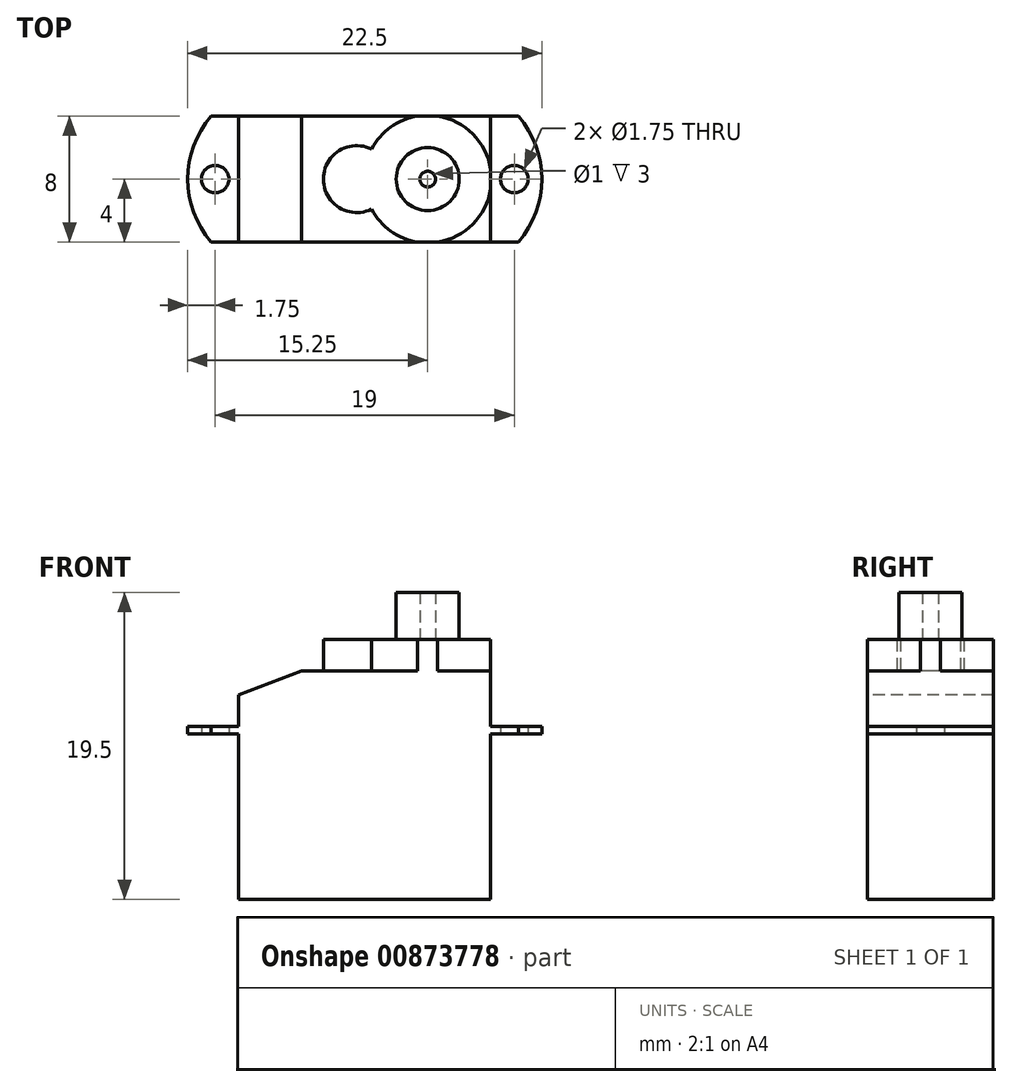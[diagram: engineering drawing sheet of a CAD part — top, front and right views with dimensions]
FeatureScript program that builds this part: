
annotation { "Feature Type Name" : "Feature", "Feature Type Description" : "" }
export const myFeature = defineFeature(function(context is Context, id is Id, definition is map)
    precondition{}
    {
        {
            var Q0;
            Q0=qCreatedBy(makeId("Top.planeOp"),FACE);
            var sketch = newSketch(context, id + "F0", { "sketchPlane" : qUnion([Q0])});
            skLineSegment(sketch, "E0.bottom", {"start": v(8, 4) * mm, "end": v(-8, 4) * mm});
            skLineSegment(sketch, "E0.top", {"start": v(8, -4) * mm, "end": v(-8, -4) * mm});
            skLineSegment(sketch, "E0.left", {"start": v(8, 4) * mm, "end": v(8, -4) * mm});
            skLineSegment(sketch, "E0.right", {"start": v(-8, 4) * mm, "end": v(-8, -4) * mm});
            skPoint(sketch, "E0.middle", {"position": v(0, 0) * mm});
            skSolve(sketch);
        }
        {
            var Q0;
            Q0 = qSketchRegion(id + "F0", true);
            extrude(context, id + "F1", {"entities" : qUnion([Q0]), "depth" : 10.5 * mm, "offsetDistance" : 25 * mm});
        }
        {
            var Q0;
            Q0=makeQuery(id+"F1.opExtrude","CAP_FACE",FACE,{"disambiguationData":[OSD([sQuery(id+"F0.wireOp",EDGE,"E0.bottom"),sQuery(id+"F0.wireOp",EDGE,"E0.top"),sQuery(id+"F0.wireOp",EDGE,"E0.left"),sQuery(id+"F0.wireOp",EDGE,"E0.right")])],"isStart":false});
            var sketch = newSketch(context, id + "F2", { "sketchPlane" : qUnion([Q0])});
            skLineSegment(sketch, "E1.bottom", {"start": v(9.75, 4) * mm, "end": v(-9.75, 4) * mm});
            skLineSegment(sketch, "E1.top", {"start": v(9.75, -4) * mm, "end": v(-9.75, -4) * mm});
            skPoint(sketch, "E1.middle", {"position": v(0, 0) * mm});
            skArc(sketch, "E2", {"start": v(-9.75, 4) * mm, "mid": v(-11.25, 0) * mm, "end": v(-9.75, -4) * mm});
            skArc(sketch, "E3", {"start": v(9.75, -4) * mm, "mid": v(11.25, 0) * mm, "end": v(9.75, 4) * mm});
            skCircle(sketch, "E4", {"center": v(-9.5, 0) * mm, "radius": 0.88 * mm});
            skCircle(sketch, "E5", {"center": v(9.5, 0) * mm, "radius": 0.88 * mm});
            skSolve(sketch);
        }
        {
            var Q0;
            Q0 = qSketchRegion(id + "F2", true);
            extrude(context, id + "F3", {"entities" : qUnion([Q0]), "operationType" : NewBodyOperationType.ADD, "depth" : 0.5 * mm, "offsetDistance" : 25 * mm});
        }
        {
            var Q0;
            Q0=makeQuery(id+"F3.opExtrude","CAP_FACE",FACE,{"disambiguationData":[OSD([sQuery(id+"F2.wireOp",EDGE,"E1.bottom"),sQuery(id+"F2.wireOp",EDGE,"E1.top"),sQuery(id+"F2.wireOp",EDGE,"E2"),sQuery(id+"F2.wireOp",EDGE,"E3"),sQuery(id+"F2.wireOp",EDGE,"E4"),sQuery(id+"F2.wireOp",EDGE,"E5")])],"isStart":false});
            var sketch = newSketch(context, id + "F4", { "sketchPlane" : qUnion([Q0])});
            skLineSegment(sketch, "E6.bottom", {"start": v(8, 4) * mm, "end": v(-8, 4) * mm});
            skLineSegment(sketch, "E6.top", {"start": v(8, -4) * mm, "end": v(-8, -4) * mm});
            skLineSegment(sketch, "E6.left", {"start": v(8, 4) * mm, "end": v(8, -4) * mm});
            skLineSegment(sketch, "E6.right", {"start": v(-8, 4) * mm, "end": v(-8, -4) * mm});
            skPoint(sketch, "E6.middle", {"position": v(0, 0) * mm});
            skSolve(sketch);
        }
        {
            var Q0;
            Q0 = qSketchRegion(id + "F4", true);
            extrude(context, id + "F5", {"entities" : qUnion([Q0]), "operationType" : NewBodyOperationType.ADD, "depth" : 3.5 * mm, "offsetDistance" : 25 * mm});
        }
        {
            var Q0;
            Q0=makeQuery(id+"F5.boolean.opBoolean","MERGE",FACE,{"derivedFrom":[makeQuery(id+"F3.boolean.opBoolean","MERGE",FACE,{"derivedFrom":[makeQuery(id+"F1.opExtrude","SWEPT_FACE",FACE,{"disambiguationData":[OSD([sQuery(id+"F0.wireOp",EDGE,"E0.top")])]}),makeQuery(id+"F3.opExtrude","SWEPT_FACE",FACE,{"disambiguationData":[OSD([sQuery(id+"F2.wireOp",EDGE,"E1.top")])]})]}),makeQuery(id+"F5.opExtrude","SWEPT_FACE",FACE,{"disambiguationData":[OSD([sQuery(id+"F4.wireOp",EDGE,"E6.top")])]})]});
            var sketch = newSketch(context, id + "F6", { "sketchPlane" : qUnion([Q0])});
            skLineSegment(sketch, "E7", {"start": v(-8, 13) * mm, "end": v(-4, 14.5) * mm});
            skLineSegment(sketch, "E8", {"start": v(-4, 14.5) * mm, "end": v(-8, 14.5) * mm});
            skLineSegment(sketch, "E9", {"start": v(-8, 14.5) * mm, "end": v(-8, 13) * mm});
            skSolve(sketch);
        }
        {
            var Q0;
            Q0 = qSketchRegion(id + "F6", true);
            extrude(context, id + "F7", {"entities" : qUnion([Q0]), "operationType" : NewBodyOperationType.REMOVE, "oppositeDirection" : true, "depth" : 25 * mm, "offsetDistance" : 25 * mm});
        }
        {
            var Q0;
            Q0=makeQuery(id+"F5.opExtrude","CAP_FACE",FACE,{"disambiguationData":[OSD([sQuery(id+"F4.wireOp",EDGE,"E6.bottom"),sQuery(id+"F4.wireOp",EDGE,"E6.top"),sQuery(id+"F4.wireOp",EDGE,"E6.left"),sQuery(id+"F4.wireOp",EDGE,"E6.right")])],"isStart":false});
            var sketch = newSketch(context, id + "F8", { "sketchPlane" : qUnion([Q0])});
            skCircle(sketch, "E10", {"center": v(4, 0) * mm, "radius": 4.05 * mm});
            skCircle(sketch, "E11", {"center": v(-0.5, 0) * mm, "radius": 2.12 * mm});
            skSolve(sketch);
        }
        {
            var Q0;
            Q0 = qSketchRegion(id + "F8", true);
            extrude(context, id + "F9", {"entities" : qUnion([Q0]), "operationType" : NewBodyOperationType.ADD, "depth" : 2 * mm, "offsetDistance" : 25 * mm});
        }
        {
            var Q0;
            {var subQ1=sQuery(id+"F8.wireOp",EDGE,"E10");Q0=makeQuery(id+"F9.boolean.opBoolean","SPLIT",FACE,{"disambiguationData":[TD([makeQuery(id+"F1.opExtrude","SWEPT_FACE",FACE,{"disambiguationData":[OSD([sQuery(id+"F0.wireOp",EDGE,"E0.bottom")])]})])],"derivedFrom":makeQuery(id+"F9.opExtrude","CAP_FACE",FACE,{"disambiguationData":[OSD([subQ1,sQuery(id+"F8.wireOp",EDGE,"E11")])],"isStart":true})});}
            extrude(context, id + "F10", {"entities" : qUnion([Q0]), "operationType" : NewBodyOperationType.REMOVE, "oppositeDirection" : true, "depth" : 25 * mm, "offsetDistance" : 25 * mm});
        }
        {
            var Q0;
            {var subQ1=sQuery(id+"F8.wireOp",EDGE,"E10");Q0=makeQuery(id+"F9.boolean.opBoolean","SPLIT",FACE,{"disambiguationData":[TD([makeQuery(id+"F1.opExtrude","SWEPT_FACE",FACE,{"disambiguationData":[OSD([sQuery(id+"F0.wireOp",EDGE,"E0.top")])]})])],"derivedFrom":makeQuery(id+"F9.opExtrude","CAP_FACE",FACE,{"disambiguationData":[OSD([subQ1,sQuery(id+"F8.wireOp",EDGE,"E11")])],"isStart":true})});}
            extrude(context, id + "F11", {"entities" : qUnion([Q0]), "operationType" : NewBodyOperationType.REMOVE, "oppositeDirection" : true, "depth" : 25 * mm, "offsetDistance" : 25 * mm});
        }
        {
            var Q0;
            {var subQ0=sQuery(id+"F4.wireOp",EDGE,"E6.left");var subQ1=sQuery(id+"F8.wireOp",EDGE,"E10");Q0=makeQuery(id+"F9.boolean.opBoolean","SPLIT",FACE,{"disambiguationData":[TD([makeQuery(id+"F5.opExtrude","SWEPT_FACE",FACE,{"disambiguationData":[OSD([subQ0])]})])],"derivedFrom":makeQuery(id+"F9.opExtrude","CAP_FACE",FACE,{"disambiguationData":[OSD([subQ1,sQuery(id+"F8.wireOp",EDGE,"E11")])],"isStart":true})});}
            extrude(context, id + "F12", {"entities" : qUnion([Q0]), "operationType" : NewBodyOperationType.REMOVE, "oppositeDirection" : true, "depth" : 25 * mm, "offsetDistance" : 25 * mm});
        }
        {
            var Q0;
            Q0=makeQuery(id+"F9.opExtrude","CAP_FACE",FACE,{"disambiguationData":[OSD([sQuery(id+"F8.wireOp",EDGE,"E10"),sQuery(id+"F8.wireOp",EDGE,"E11")])],"isStart":false});
            var sketch = newSketch(context, id + "F13", { "sketchPlane" : qUnion([Q0])});
            skCircle(sketch, "E12", {"center": v(4, 0) * mm, "radius": 2 * mm});
            skCircle(sketch, "E13", {"center": v(4, 0) * mm, "radius": 0.5 * mm});
            skSolve(sketch);
        }
        {
            var Q0;
            Q0 = qSketchRegion(id + "F13", true);
            extrude(context, id + "F14", {"entities" : qUnion([Q0]), "operationType" : NewBodyOperationType.ADD, "depth" : 3 * mm, "offsetDistance" : 25 * mm});
        }
    });
